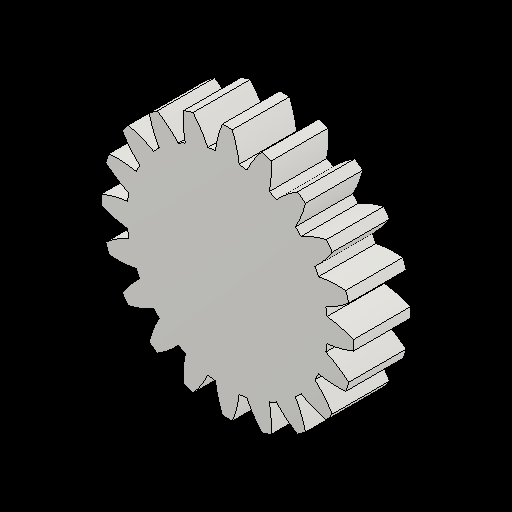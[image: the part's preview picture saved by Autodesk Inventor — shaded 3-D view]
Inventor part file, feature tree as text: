
AUTODESK INVENTOR PART (.ipt)
format: ipt  version: 2023.2 (Build 272271030, 271C)  size: 205,824 bytes
history: native  units: mm (DEFAULTED — no unit token found)
features: plane x3, other x3, sketch x2, extrude x1
ambient origin geometry x8: Origin, YZ Plane, XZ Plane, XY Plane, X Axis, Y Axis, Z Axis, Center Point
bodies: Solid1 (feature_tree)
feature tree (9):
  extrude  "Extrusion1"  Depth=5.0mm TaperAngle=0.0deg
  plane  "Work Plane2"
  plane  "Work Plane8"
  plane  "Work Plane9"
  other  "Spur Gear"
  sketch  "Sketch1"  dims[d0=22.0mm d1=5.0mm d2=0.0mm]
  sketch  "Sketch2"  dims[d3=20.0mm d4=10.0mm d5=0.0mm d16=14.0mm d17=0.0mm d34=1.570796mm d39=0.0mm d41=0.0mm d43=14.0mm d46=14.0mm d47=0.0mm d48=0.0mm]
  other  "Srf1"
  other  "Pitch Diameter"
